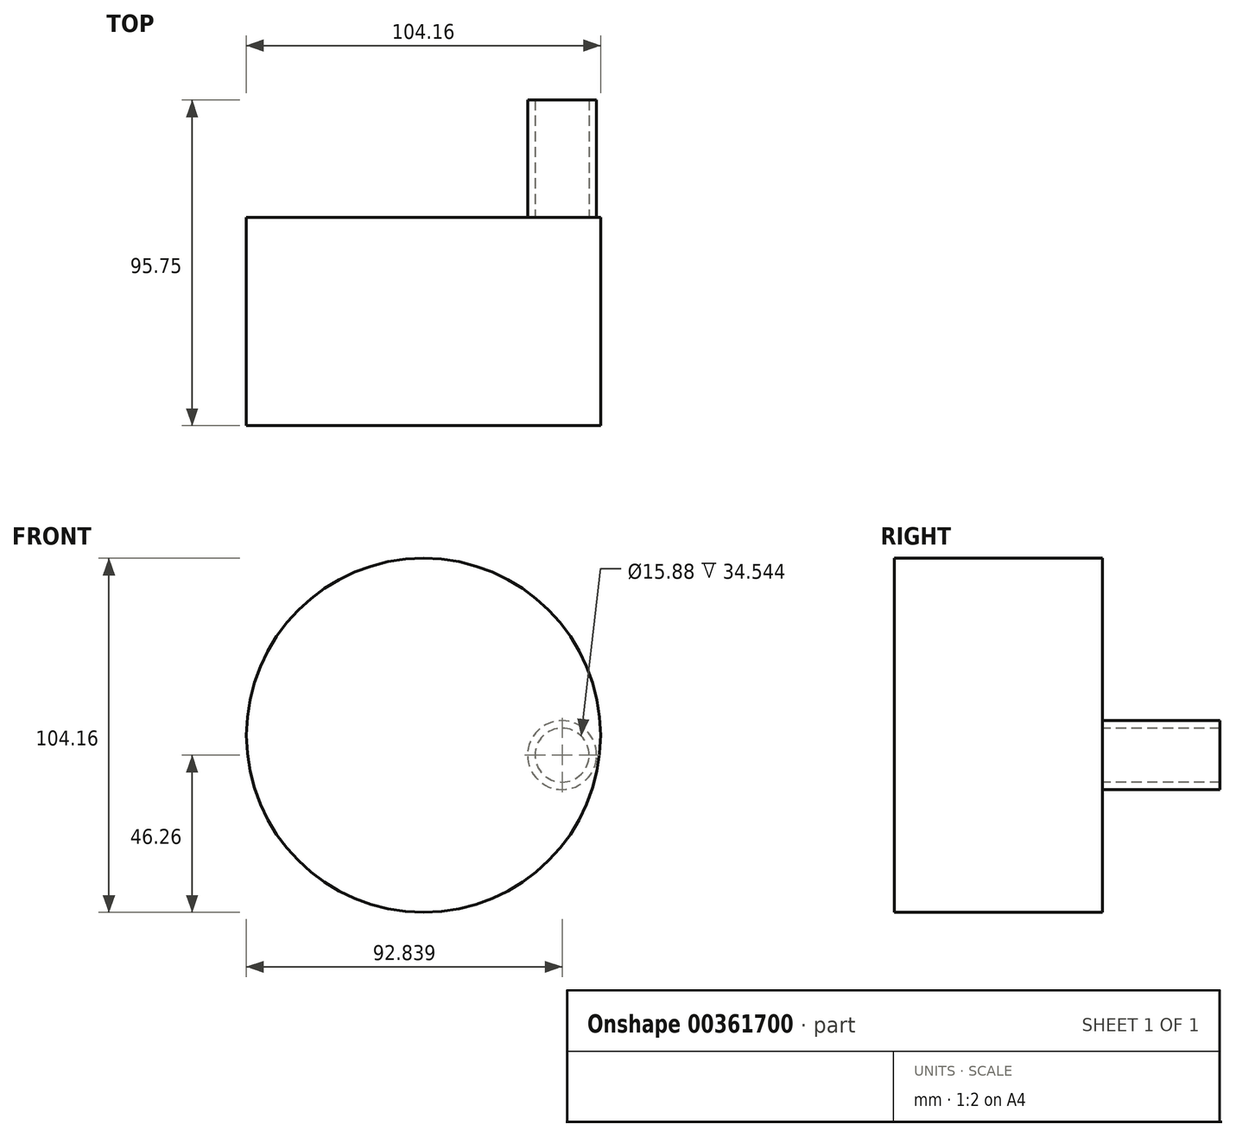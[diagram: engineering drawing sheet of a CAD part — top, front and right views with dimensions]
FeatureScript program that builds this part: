
annotation { "Feature Type Name" : "Feature", "Feature Type Description" : "" }
export const myFeature = defineFeature(function(context is Context, id is Id, definition is map)
    precondition{}
    {
        {
            var Q0;
            Q0=qCreatedBy(makeId("Front.planeOp"),FACE);
            var sketch = newSketch(context, id + "F0", { "sketchPlane" : qUnion([Q0])});
            skCircle(sketch, "E0", {"center": v(0, 0) * mm, "radius": 52.08 * mm});
            skSolve(sketch);
        }
        {
            var Q0;
            Q0=makeQuery(id+"F0.imprint","IMPRINT",FACE,{"disambiguationData":[TD([[makeQuery(id+"F0.imprint","IMPRINT",EDGE,{"derivedFrom":sQuery(id+"F0.wireOp",EDGE,"E0")}),1.0]])]});
            extrude(context, id + "F1", {"entities" : qUnion([Q0]), "depth" : 61.2 * mm});
        }
        {
            var Q0;
            Q0=makeQuery(id+"F1.opExtrude","CAP_FACE",FACE,{"disambiguationData":[OSD([sQuery(id+"F0.wireOp",EDGE,"E0")])],"isStart":true});
            var sketch = newSketch(context, id + "F2", { "sketchPlane" : qUnion([Q0])});
            skCircle(sketch, "E1", {"center": v(-40.76, -5.82) * mm, "radius": 7.94 * mm});
            skCircle(sketch, "E2", {"center": v(-40.76, -5.82) * mm, "radius": 10.12 * mm});
            skSolve(sketch);
        }
        {
            var Q0;
            Q0 = qSketchRegion(id + "F2", true);
            extrude(context, id + "F3", {"entities" : qUnion([Q0]), "operationType" : NewBodyOperationType.ADD, "depth" : 34.54 * mm});
        }
    });
